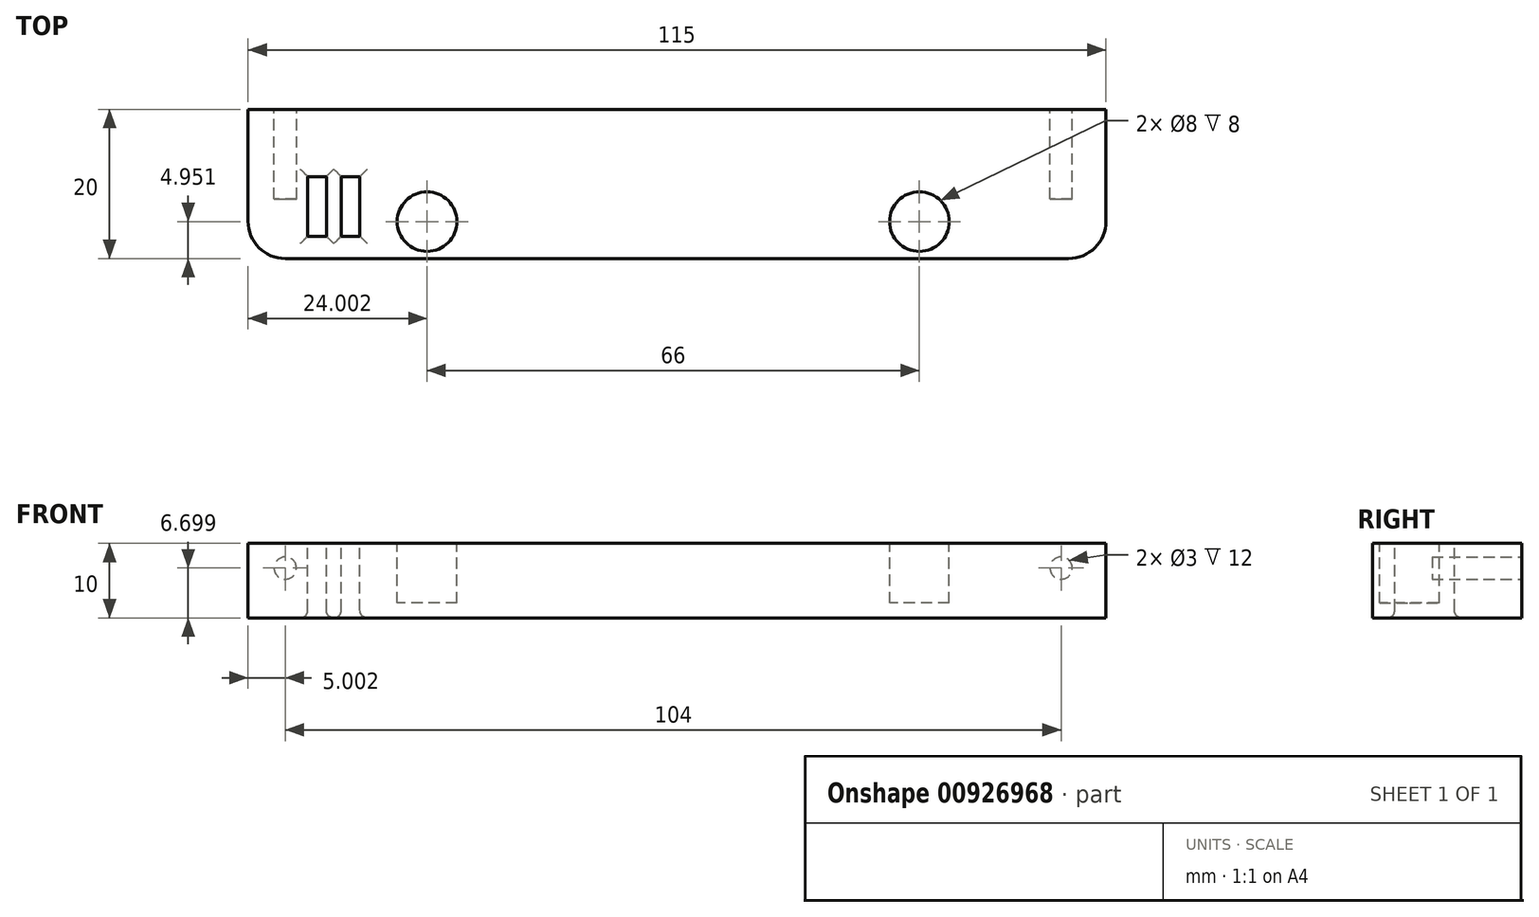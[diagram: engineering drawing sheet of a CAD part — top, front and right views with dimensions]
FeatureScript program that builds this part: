
annotation { "Feature Type Name" : "Feature", "Feature Type Description" : "" }
export const myFeature = defineFeature(function(context is Context, id is Id, definition is map)
    precondition{}
    {
        {
            var Q0;
            Q0=qCreatedBy(makeId("Top.planeOp"),FACE);
            var sketch = newSketch(context, id + "F0", { "sketchPlane" : qUnion([Q0])});
            skLineSegment(sketch, "E0.bottom", {"start": v(-59.06, -1.73) * mm, "end": v(55.94, -1.73) * mm});
            skLineSegment(sketch, "E0.top", {"start": v(-59.06, -21.73) * mm, "end": v(55.94, -21.73) * mm});
            skLineSegment(sketch, "E0.left", {"start": v(-59.06, -1.73) * mm, "end": v(-59.06, -21.73) * mm});
            skLineSegment(sketch, "E0.right", {"start": v(55.94, -1.73) * mm, "end": v(55.94, -21.73) * mm});
            skSolve(sketch);
        }
        {
            var Q0;
            Q0 = qSketchRegion(id + "F0", true);
            extrude(context, id + "F1", {"entities" : qUnion([Q0]), "depth" : 10 * mm, "offsetDistance" : 25 * mm});
        }
        {
            var Q0;
            Q0=makeQuery(id+"F1.opExtrude","CAP_FACE",FACE,{"disambiguationData":[OSD([sQuery(id+"F0.wireOp",EDGE,"E0.bottom"),sQuery(id+"F0.wireOp",EDGE,"E0.top"),sQuery(id+"F0.wireOp",EDGE,"E0.left"),sQuery(id+"F0.wireOp",EDGE,"E0.right")])],"isStart":false});
            var sketch = newSketch(context, id + "F2", { "sketchPlane" : qUnion([Q0])});
            skCircle(sketch, "E1", {"center": v(-35.06, -16.78) * mm, "radius": 4 * mm});
            skCircle(sketch, "E2", {"center": v(30.94, -16.78) * mm, "radius": 4 * mm});
            skLineSegment(sketch, "E3", {"start": v(-61.7, -16.78) * mm, "end": v(87.9, -16.78) * mm, "construction": true});
            skSolve(sketch);
        }
        {
            var Q0;
            Q0 = qSketchRegion(id + "F2", true);
            extrude(context, id + "F3", {"entities" : qUnion([Q0]), "operationType" : NewBodyOperationType.REMOVE, "oppositeDirection" : true, "depth" : 8 * mm, "offsetDistance" : 25 * mm});
        }
        {
            var Q0;
            Q0=makeQuery(id+"F1.opExtrude","SWEPT_FACE",FACE,{"disambiguationData":[OSD([sQuery(id+"F0.wireOp",EDGE,"E0.bottom")])]});
            var sketch = newSketch(context, id + "F4", { "sketchPlane" : qUnion([Q0])});
            skCircle(sketch, "E4", {"center": v(54.06, 6.7) * mm, "radius": 1.5 * mm});
            skCircle(sketch, "E5", {"center": v(-49.94, 6.7) * mm, "radius": 1.5 * mm});
            skLineSegment(sketch, "E6", {"start": v(59.48, 6.7) * mm, "end": v(-55.52, 6.7) * mm, "construction": true});
            skSolve(sketch);
        }
        {
            var Q0;
            Q0 = qSketchRegion(id + "F4", true);
            extrude(context, id + "F5", {"entities" : qUnion([Q0]), "operationType" : NewBodyOperationType.REMOVE, "oppositeDirection" : true, "depth" : 12 * mm, "offsetDistance" : 25 * mm});
        }
        {
            var Q0;
            Q0=makeQuery(id+"F1.opExtrude","SWEPT_EDGE",EDGE,{"disambiguationData":[OSD([sQuery(id+"F0.wireOp",EDGE,"E0.top"),sQuery(id+"F0.wireOp",EDGE,"E0.left")])]});
            var Q1;
            Q1=makeQuery(id+"F1.opExtrude","SWEPT_EDGE",EDGE,{"disambiguationData":[OSD([sQuery(id+"F0.wireOp",EDGE,"E0.top"),sQuery(id+"F0.wireOp",EDGE,"E0.right")])]});
            fillet(context, id + "F6", {"entities" : qUnion([Q0, Q1]), "radius" : 5 * mm, "tangentPropagation" : true, "allowEdgeOverflow" : false});
        }
        {
            var Q0;
            Q0=makeQuery(id+"F1.opExtrude","CAP_FACE",FACE,{"disambiguationData":[OSD([sQuery(id+"F0.wireOp",EDGE,"E0.bottom"),sQuery(id+"F0.wireOp",EDGE,"E0.top"),sQuery(id+"F0.wireOp",EDGE,"E0.left"),sQuery(id+"F0.wireOp",EDGE,"E0.right")])],"isStart":false});
            var sketch = newSketch(context, id + "F7", { "sketchPlane" : qUnion([Q0])});
            skLineSegment(sketch, "E7.bottom", {"start": v(-51.06, -10.73) * mm, "end": v(-48.56, -10.73) * mm});
            skLineSegment(sketch, "E7.top", {"start": v(-51.06, -18.73) * mm, "end": v(-48.56, -18.73) * mm});
            skLineSegment(sketch, "E7.left", {"start": v(-51.06, -10.73) * mm, "end": v(-51.06, -18.73) * mm});
            skLineSegment(sketch, "E7.right", {"start": v(-48.56, -10.73) * mm, "end": v(-48.56, -18.73) * mm});
            skLineSegment(sketch, "E8.bottom", {"start": v(-46.56, -10.73) * mm, "end": v(-44.06, -10.73) * mm});
            skLineSegment(sketch, "E8.top", {"start": v(-46.56, -18.73) * mm, "end": v(-44.06, -18.73) * mm});
            skLineSegment(sketch, "E8.left", {"start": v(-46.56, -10.73) * mm, "end": v(-46.56, -18.73) * mm});
            skLineSegment(sketch, "E8.right", {"start": v(-44.06, -10.73) * mm, "end": v(-44.06, -18.73) * mm});
            skSolve(sketch);
        }
        {
            var Q0;
            Q0 = qSketchRegion(id + "F7", true);
            extrude(context, id + "F8", {"entities" : qUnion([Q0]), "operationType" : NewBodyOperationType.REMOVE, "oppositeDirection" : true, "depth" : 25 * mm, "offsetDistance" : 25 * mm});
        }
        {
            var Q0;
            Q0=makeQuery(id+"F8.boolean.opBoolean","COPY",EDGE,{"derivedFrom":makeQuery(id+"F8.opExtrude","CAP_EDGE",EDGE,{"disambiguationData":[OSD([sQuery(id+"F7.wireOp",EDGE,"E7.left")])],"isStart":true})});
            var Q1;
            Q1=makeQuery(id+"F8.boolean.opBoolean","COPY",EDGE,{"derivedFrom":makeQuery(id+"F8.opExtrude","CAP_EDGE",EDGE,{"disambiguationData":[OSD([sQuery(id+"F7.wireOp",EDGE,"E7.bottom")])],"isStart":true})});
            var Q2;
            Q2=makeQuery(id+"F8.boolean.opBoolean","COPY",EDGE,{"derivedFrom":makeQuery(id+"F8.opExtrude","CAP_EDGE",EDGE,{"disambiguationData":[OSD([sQuery(id+"F7.wireOp",EDGE,"E7.right")])],"isStart":true})});
            var Q3;
            Q3=makeQuery(id+"F8.boolean.opBoolean","COPY",EDGE,{"derivedFrom":makeQuery(id+"F8.opExtrude","CAP_EDGE",EDGE,{"disambiguationData":[OSD([sQuery(id+"F7.wireOp",EDGE,"E7.top")])],"isStart":true})});
            var Q4;
            Q4=makeQuery(id+"F8.boolean.opBoolean","COPY",EDGE,{"derivedFrom":makeQuery(id+"F8.opExtrude","CAP_EDGE",EDGE,{"disambiguationData":[OSD([sQuery(id+"F7.wireOp",EDGE,"E8.top")])],"isStart":true})});
            var Q5;
            Q5=makeQuery(id+"F8.boolean.opBoolean","COPY",EDGE,{"derivedFrom":makeQuery(id+"F8.opExtrude","CAP_EDGE",EDGE,{"disambiguationData":[OSD([sQuery(id+"F7.wireOp",EDGE,"E8.left")])],"isStart":true})});
            var Q6;
            Q6=makeQuery(id+"F8.boolean.opBoolean","COPY",EDGE,{"derivedFrom":makeQuery(id+"F8.opExtrude","CAP_EDGE",EDGE,{"disambiguationData":[OSD([sQuery(id+"F7.wireOp",EDGE,"E8.bottom")])],"isStart":true})});
            var Q7;
            Q7=makeQuery(id+"F8.boolean.opBoolean","COPY",EDGE,{"derivedFrom":makeQuery(id+"F8.opExtrude","CAP_EDGE",EDGE,{"disambiguationData":[OSD([sQuery(id+"F7.wireOp",EDGE,"E8.right")])],"isStart":true})});
            var Q8;
            Q8=makeQuery(id+"F8.boolean.opBoolean","INTERSECT",EDGE,{"derivedFrom":[makeQuery(id+"F1.opExtrude","CAP_FACE",FACE,{"disambiguationData":[OSD([sQuery(id+"F0.wireOp",EDGE,"E0.bottom"),sQuery(id+"F0.wireOp",EDGE,"E0.top"),sQuery(id+"F0.wireOp",EDGE,"E0.left"),sQuery(id+"F0.wireOp",EDGE,"E0.right")])],"isStart":true}),makeQuery(id+"F8.opExtrude","SWEPT_FACE",FACE,{"disambiguationData":[OSD([sQuery(id+"F7.wireOp",EDGE,"E8.right")])]})]});
            var Q9;
            Q9=makeQuery(id+"F8.boolean.opBoolean","INTERSECT",EDGE,{"derivedFrom":[makeQuery(id+"F1.opExtrude","CAP_FACE",FACE,{"disambiguationData":[OSD([sQuery(id+"F0.wireOp",EDGE,"E0.bottom"),sQuery(id+"F0.wireOp",EDGE,"E0.top"),sQuery(id+"F0.wireOp",EDGE,"E0.left"),sQuery(id+"F0.wireOp",EDGE,"E0.right")])],"isStart":true}),makeQuery(id+"F8.opExtrude","SWEPT_FACE",FACE,{"disambiguationData":[OSD([sQuery(id+"F7.wireOp",EDGE,"E8.bottom")])]})]});
            var Q10;
            Q10=makeQuery(id+"F8.boolean.opBoolean","INTERSECT",EDGE,{"derivedFrom":[makeQuery(id+"F1.opExtrude","CAP_FACE",FACE,{"disambiguationData":[OSD([sQuery(id+"F0.wireOp",EDGE,"E0.bottom"),sQuery(id+"F0.wireOp",EDGE,"E0.top"),sQuery(id+"F0.wireOp",EDGE,"E0.left"),sQuery(id+"F0.wireOp",EDGE,"E0.right")])],"isStart":true}),makeQuery(id+"F8.opExtrude","SWEPT_FACE",FACE,{"disambiguationData":[OSD([sQuery(id+"F7.wireOp",EDGE,"E8.left")])]})]});
            var Q11;
            Q11=makeQuery(id+"F8.boolean.opBoolean","INTERSECT",EDGE,{"derivedFrom":[makeQuery(id+"F1.opExtrude","CAP_FACE",FACE,{"disambiguationData":[OSD([sQuery(id+"F0.wireOp",EDGE,"E0.bottom"),sQuery(id+"F0.wireOp",EDGE,"E0.top"),sQuery(id+"F0.wireOp",EDGE,"E0.left"),sQuery(id+"F0.wireOp",EDGE,"E0.right")])],"isStart":true}),makeQuery(id+"F8.opExtrude","SWEPT_FACE",FACE,{"disambiguationData":[OSD([sQuery(id+"F7.wireOp",EDGE,"E8.top")])]})]});
            var Q12;
            Q12=makeQuery(id+"F8.boolean.opBoolean","INTERSECT",EDGE,{"derivedFrom":[makeQuery(id+"F1.opExtrude","CAP_FACE",FACE,{"disambiguationData":[OSD([sQuery(id+"F0.wireOp",EDGE,"E0.bottom"),sQuery(id+"F0.wireOp",EDGE,"E0.top"),sQuery(id+"F0.wireOp",EDGE,"E0.left"),sQuery(id+"F0.wireOp",EDGE,"E0.right")])],"isStart":true}),makeQuery(id+"F8.opExtrude","SWEPT_FACE",FACE,{"disambiguationData":[OSD([sQuery(id+"F7.wireOp",EDGE,"E7.top")])]})]});
            var Q13;
            Q13=makeQuery(id+"F8.boolean.opBoolean","INTERSECT",EDGE,{"derivedFrom":[makeQuery(id+"F1.opExtrude","CAP_FACE",FACE,{"disambiguationData":[OSD([sQuery(id+"F0.wireOp",EDGE,"E0.bottom"),sQuery(id+"F0.wireOp",EDGE,"E0.top"),sQuery(id+"F0.wireOp",EDGE,"E0.left"),sQuery(id+"F0.wireOp",EDGE,"E0.right")])],"isStart":true}),makeQuery(id+"F8.opExtrude","SWEPT_FACE",FACE,{"disambiguationData":[OSD([sQuery(id+"F7.wireOp",EDGE,"E7.right")])]})]});
            var Q14;
            Q14=makeQuery(id+"F8.boolean.opBoolean","INTERSECT",EDGE,{"derivedFrom":[makeQuery(id+"F1.opExtrude","CAP_FACE",FACE,{"disambiguationData":[OSD([sQuery(id+"F0.wireOp",EDGE,"E0.bottom"),sQuery(id+"F0.wireOp",EDGE,"E0.top"),sQuery(id+"F0.wireOp",EDGE,"E0.left"),sQuery(id+"F0.wireOp",EDGE,"E0.right")])],"isStart":true}),makeQuery(id+"F8.opExtrude","SWEPT_FACE",FACE,{"disambiguationData":[OSD([sQuery(id+"F7.wireOp",EDGE,"E7.bottom")])]})]});
            var Q15;
            Q15=makeQuery(id+"F8.boolean.opBoolean","INTERSECT",EDGE,{"derivedFrom":[makeQuery(id+"F1.opExtrude","CAP_FACE",FACE,{"disambiguationData":[OSD([sQuery(id+"F0.wireOp",EDGE,"E0.bottom"),sQuery(id+"F0.wireOp",EDGE,"E0.top"),sQuery(id+"F0.wireOp",EDGE,"E0.left"),sQuery(id+"F0.wireOp",EDGE,"E0.right")])],"isStart":true}),makeQuery(id+"F8.opExtrude","SWEPT_FACE",FACE,{"disambiguationData":[OSD([sQuery(id+"F7.wireOp",EDGE,"E7.left")])]})]});
            fillet(context, id + "F9", {"entities" : qUnion([Q0, Q1, Q2, Q3, Q4, Q5, Q6, Q7, Q8, Q9, Q10, Q11, Q12, Q13, Q14, Q15]), "radius" : 1 * mm, "tangentPropagation" : true, "allowEdgeOverflow" : false});
        }
    });
